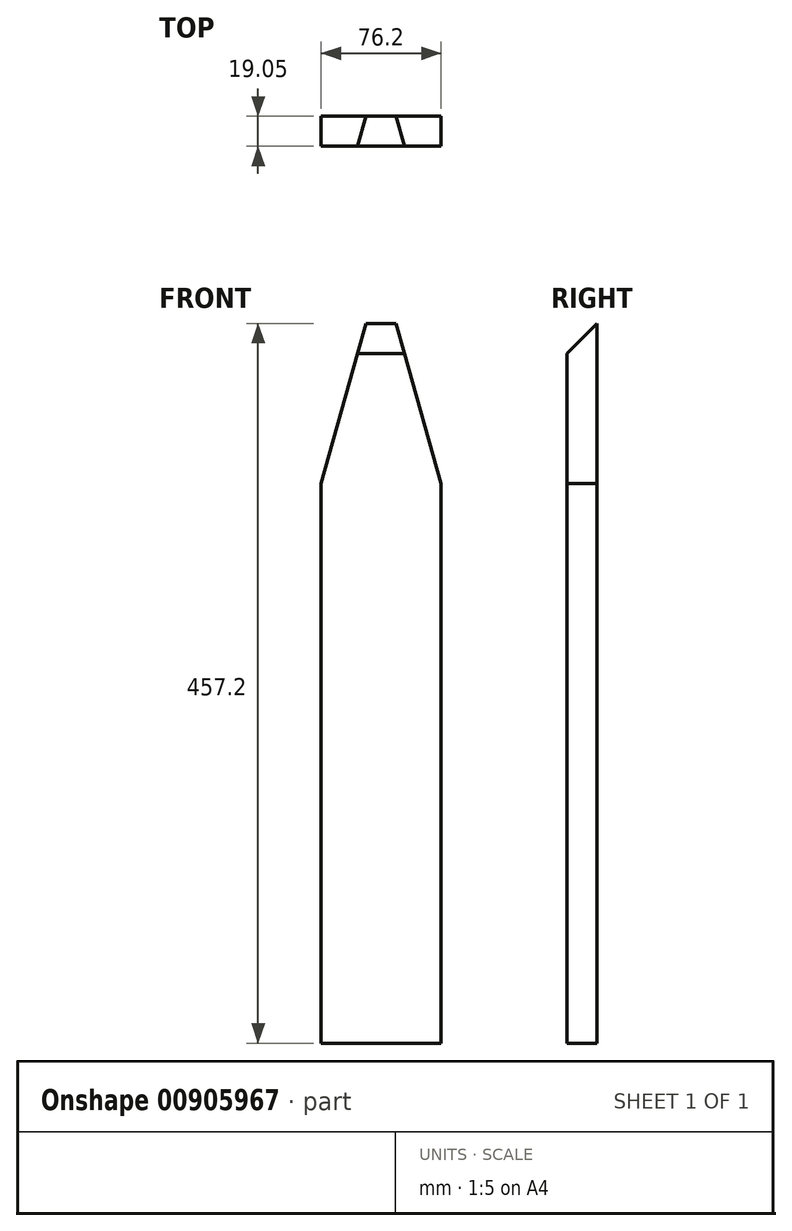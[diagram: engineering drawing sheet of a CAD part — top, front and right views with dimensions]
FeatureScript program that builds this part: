
annotation { "Feature Type Name" : "Feature", "Feature Type Description" : "" }
export const myFeature = defineFeature(function(context is Context, id is Id, definition is map)
    precondition{}
    {
        {
            var Q0;
            Q0=qCreatedBy(makeId("Front.planeOp"),FACE);
            var sketch = newSketch(context, id + "F0", { "sketchPlane" : qUnion([Q0])});
            skLineSegment(sketch, "E0.bottom", {"start": v(0, 0) * mm, "end": v(76.2, 0) * mm});
            skLineSegment(sketch, "E0.top", {"start": v(0, 457.2) * mm, "end": v(76.2, 457.2) * mm});
            skLineSegment(sketch, "E0.left", {"start": v(0, 0) * mm, "end": v(0, 457.2) * mm});
            skLineSegment(sketch, "E0.right", {"start": v(76.2, 0) * mm, "end": v(76.2, 457.2) * mm});
            skSolve(sketch);
        }
        {
            var Q0;
            Q0 = qSketchRegion(id + "F0", true);
            extrude(context, id + "F1", {"entities" : qUnion([Q0]), "depth" : 19.05 * mm, "offsetDistance" : 25.4 * mm});
        }
        {
            var Q0;
            Q0=makeQuery(id+"F1.opExtrude","CAP_FACE",FACE,{"disambiguationData":[OSD([sQuery(id+"F0.wireOp",EDGE,"E0.bottom"),sQuery(id+"F0.wireOp",EDGE,"E0.top"),sQuery(id+"F0.wireOp",EDGE,"E0.left"),sQuery(id+"F0.wireOp",EDGE,"E0.right")])],"isStart":false});
            var sketch = newSketch(context, id + "F2", { "sketchPlane" : qUnion([Q0])});
            skLineSegment(sketch, "E1", {"start": v(28.57, 457.2) * mm, "end": v(0, 355.6) * mm});
            skLineSegment(sketch, "E2", {"start": v(47.62, 457.2) * mm, "end": v(76.2, 355.6) * mm});
            skLineSegment(sketch, "E3", {"start": v(76.2, 355.6) * mm, "end": v(76.2, 457.2) * mm});
            skLineSegment(sketch, "E4", {"start": v(76.2, 457.2) * mm, "end": v(47.62, 457.2) * mm});
            skLineSegment(sketch, "E5", {"start": v(0, 355.6) * mm, "end": v(0, 457.2) * mm});
            skLineSegment(sketch, "E6", {"start": v(0, 457.2) * mm, "end": v(28.57, 457.2) * mm});
            skSolve(sketch);
        }
        {
            var Q0;
            Q0 = qSketchRegion(id + "F2", true);
            extrude(context, id + "F3", {"entities" : qUnion([Q0]), "operationType" : NewBodyOperationType.REMOVE, "endBound" : BoundingType.THROUGH_ALL, "oppositeDirection" : true, "depth" : 25.4 * mm, "offsetDistance" : 25.4 * mm});
        }
        {
            var Q0;
            Q0=makeQuery(id+"F1.opExtrude","CAP_EDGE",EDGE,{"disambiguationData":[OSD([sQuery(id+"F0.wireOp",EDGE,"E0.top")])],"isStart":false});
            chamfer(context, id + "F4", {"entities" : qUnion([Q0]), "width" : 19.05 * mm, "tangentPropagation" : true});
        }
    });
